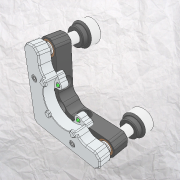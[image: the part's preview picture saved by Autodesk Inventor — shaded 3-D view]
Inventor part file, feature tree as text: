
AUTODESK INVENTOR PART (.ipt)
format: ipt  version: 2020 (Build 240168000, 168)  size: 3,613,184 bytes
history: native  units: in
note: dims shown in document units (in); Inventor stores cm internally (conversion verified against a paired STEP export)
features: other x22, projected_geometry x13, sketch x1
ambient origin geometry x8: Origin, YZ Plane, XZ Plane, XY Plane, X Axis, Y Axis, Z Axis, Center Point
bodies: Solid1 (feature_tree), Solid2 (feature_tree), Solid3 (feature_tree), Solid4 (feature_tree), Solid5 (feature_tree), Solid6 (feature_tree), Solid7 (feature_tree), Solid8 (feature_tree), Solid9 (feature_tree), Solid10 (feature_tree), Solid11 (feature_tree), Solid12 (feature_tree), Solid13 (feature_tree), Solid14 (feature_tree), Solid15 (feature_tree), Solid16 (feature_tree), Solid17 (feature_tree), Solid18 (feature_tree), Solid19 (feature_tree), Solid20 (feature_tree), Solid21 (feature_tree), Solid22 (feature_tree)
feature tree (36):
  sketch  "Sketch1"
  projected_geometry  "Projected Loop1"
  projected_geometry  "Projected Loop2"
  projected_geometry  "Projected Loop3"
  projected_geometry  "Projected Loop4"
  projected_geometry  "Projected Loop5"
  projected_geometry  "Projected Loop6"
  projected_geometry  "Projected Loop7"
  projected_geometry  "Projected Loop8"
  projected_geometry  "Projected Loop9"
  projected_geometry  "Projected Loop10"
  projected_geometry  "Projected Loop11"
  projected_geometry  "Projected Loop12"
  projected_geometry  "Projected Loop13"
  other  "6628-001-1-solid1"
  other  "0017-001-1-solid1"
  other  "0806-001-1-solid1"
  other  "1579-004-1-solid1"
  other  "BALL1875GR100-1-solid1"
  other  "BALL3125GR100-1-solid1"
  other  "DOWEL0625X250-1-solid1"
  other  "TTN034686-1-solid1"
  other  "0017-001-2-solid1"
  other  "0806-001-2-solid1"
  other  "1579-004-2-solid1"
  other  "BALL1875GR100-2-solid1"
  other  "DOWEL0625X250-2-solid1"
  other  "W25H042-1-solid1"
  other  "DOWEL0625X375-3-solid1"
  other  "DOWEL0625X375-4-solid1"
  other  "SS4N019-1-1-solid1"
  other  "SS4N019-1-2-solid1"
  other  "KM2 SPRING ASSY-1_SPRG-KM1-1-solid1"
  other  "SPRG-KM1-1-solid1"
  other  "SS6S025-1-1-solid1"
  other  "SS6S025-1-2-solid1"
